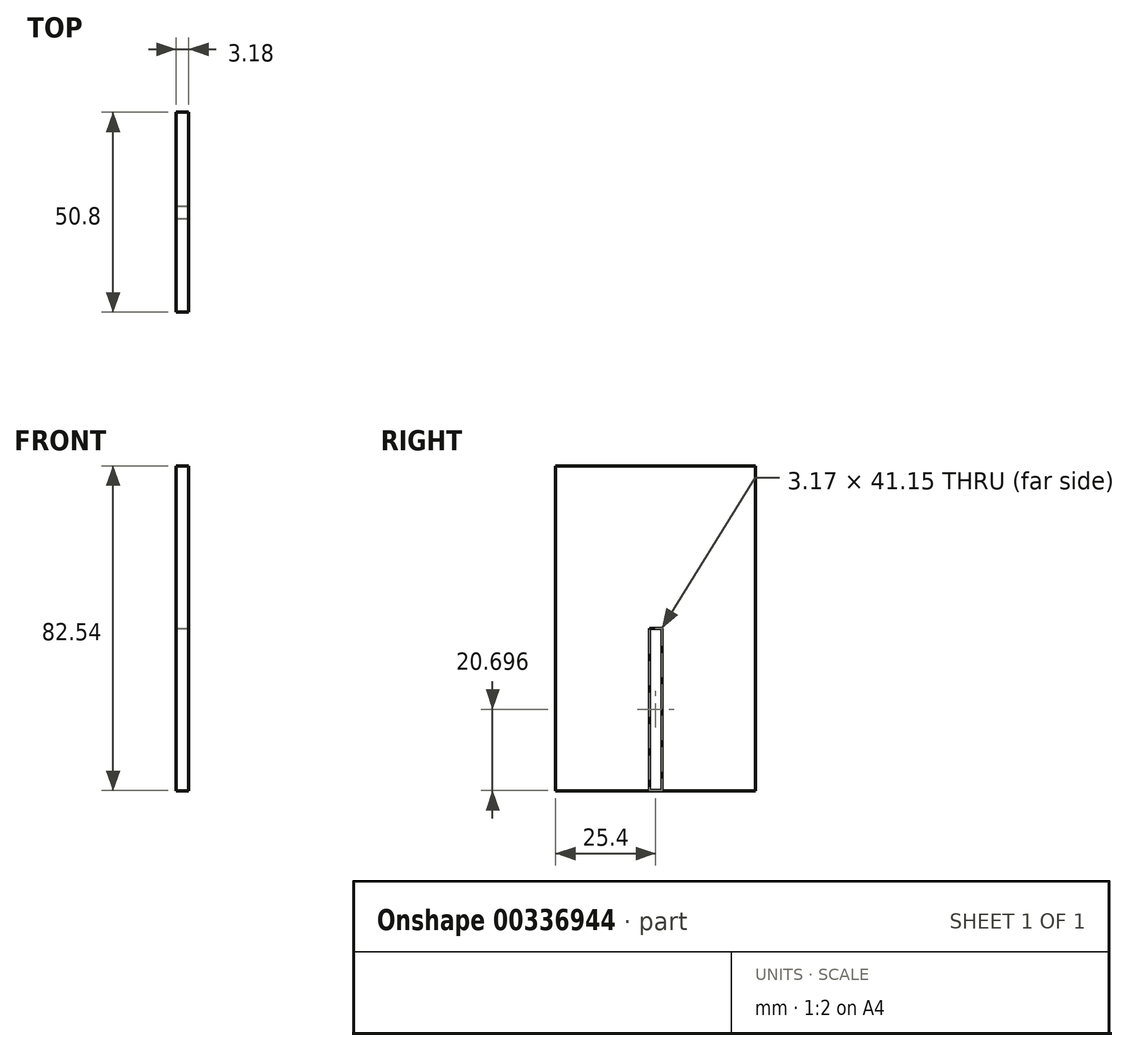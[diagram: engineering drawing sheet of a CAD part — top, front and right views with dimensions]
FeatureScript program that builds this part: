
annotation { "Feature Type Name" : "Feature", "Feature Type Description" : "" }
export const myFeature = defineFeature(function(context is Context, id is Id, definition is map)
    precondition{}
    {
        {
            var Q0;
            Q0=qCreatedBy(makeId("Right.planeOp"),FACE);
            var sketch = newSketch(context, id + "F0", { "sketchPlane" : qUnion([Q0])});
            skLineSegment(sketch, "E0.bottom", {"start": v(25.4, 41.28) * mm, "end": v(-25.4, 41.28) * mm});
            skLineSegment(sketch, "E0.top", {"start": v(25.4, -41.28) * mm, "end": v(-25.4, -41.28) * mm});
            skLineSegment(sketch, "E0.left", {"start": v(25.4, 41.28) * mm, "end": v(25.4, -41.28) * mm});
            skLineSegment(sketch, "E0.right", {"start": v(-25.4, 41.28) * mm, "end": v(-25.4, -41.28) * mm});
            skPoint(sketch, "E0.middle", {"position": v(0, 0) * mm});
            skSolve(sketch);
        }
        {
            var Q0;
            Q0=makeQuery(id+"F0.imprint","IMPRINT",FACE,{"disambiguationData":[TD([[makeQuery(id+"F0.imprint","IMPRINT",EDGE,{"derivedFrom":sQuery(id+"F0.wireOp",EDGE,"E0.bottom")}),1.0]])]});
            extrude(context, id + "F1", {"entities" : qUnion([Q0]), "depth" : 3.17 * mm});
        }
        {
            var Q0;
            Q0=makeQuery(id+"F1.opExtrude","CAP_FACE",FACE,{"disambiguationData":[OSD([sQuery(id+"F0.wireOp",EDGE,"E0.bottom"),sQuery(id+"F0.wireOp",EDGE,"E0.top"),sQuery(id+"F0.wireOp",EDGE,"E0.left"),sQuery(id+"F0.wireOp",EDGE,"E0.right")])],"isStart":false});
            var sketch = newSketch(context, id + "F2", { "sketchPlane" : qUnion([Q0])});
            skLineSegment(sketch, "E1.bottom", {"start": v(1.59, 0) * mm, "end": v(-1.59, 0) * mm});
            skLineSegment(sketch, "E1.top", {"start": v(1.59, -41.15) * mm, "end": v(-1.59, -41.15) * mm});
            skLineSegment(sketch, "E1.left", {"start": v(1.59, 0) * mm, "end": v(1.59, -41.15) * mm});
            skLineSegment(sketch, "E1.right", {"start": v(-1.59, 0) * mm, "end": v(-1.59, -41.15) * mm});
            skPoint(sketch, "E1.middle", {"position": v(0, -20.57) * mm});
            skSolve(sketch);
        }
        {
            var Q0;
            Q0=makeQuery(id+"F2.imprint","IMPRINT",FACE,{"disambiguationData":[TD([[makeQuery(id+"F2.imprint","IMPRINT",EDGE,{"derivedFrom":sQuery(id+"F2.wireOp",EDGE,"E1.bottom")}),1.0]])]});
            extrude(context, id + "F3", {"entities" : qUnion([Q0]), "operationType" : NewBodyOperationType.REMOVE, "oppositeDirection" : true, "depth" : 25.4 * mm});
        }
    });
